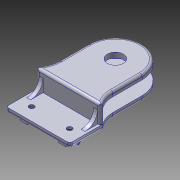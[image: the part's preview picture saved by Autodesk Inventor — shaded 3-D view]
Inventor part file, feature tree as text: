
AUTODESK INVENTOR PART (.ipt)
format: ipt  version: 2013 (Build 170138000, 138)  size: 346,112 bytes
history: native  units: mm
features: extrude x8, sketch x8, fillet x4, hole x1, chamfer x1, mirror x1
ambient origin geometry x8: Origin, YZ Plane, XZ Plane, XY Plane, X Axis, Y Axis, Z Axis, Center Point
bodies: Solid1 (feature_tree)
feature tree (23):
  extrude  "Extrusion1"  Depth=17.5mm
  sketch  "Sketch2"  dims[d3=6.35mm d4=10.5mm]
  extrude  "Extrusion2"  Depth=10.5mm
  extrude  "Extrusion3"  Depth=2.0mm
  extrude  "Extrusion4"  Depth=25.0mm
  sketch  "Sketch6"  dims[d12=1.0mm d13=0.0mm d14=2.0mm]
  hole  "Hole1"  [1 undecoded]
  extrude  "Extrusion5"  Depth=5.0mm
  extrude  "Extrusion6"  Depth=5.0mm
  extrude  "Extrusion7"  Depth=1.0mm TaperAngle=0.0deg
  chamfer  "Chamfer1"  Distance=0.5mm
  mirror  "Mirror1"
  fillet  "Fillet1"  Radius=1.0mm
  fillet  "Fillet2"  Radius=1.0mm
  fillet  "Fillet3"  Radius=1.0mm
  extrude  "Extrusion8"  Depth=1.0mm TaperAngle=45.0deg
  fillet  "Fillet4"  Radius=10.5mm
  sketch  "Sketch1"  dims[d0=21.0mm d2=17.5mm]
  sketch  "Sketch3"  dims[d5=9.35mm d6=0.0mm d7=2.0mm]
  sketch  "Sketch4"  dims[d8=2.0mm d9=0.0mm d10=25.0mm]
  sketch  "Sketch7"  dims[d16=12.0mm d17=0.0mm d18=5.0mm]
  sketch  "Sketch8"  dims[d19=5.0mm d20=5.0mm]
  sketch  "Sketch9"  dims[d21=2.013mm d22=6.0mm d23=3.023mm d24=2.0mm d25=14.3117mm d26=8.0mm d27=20.594885mm d28=1.0mm d29=0.0mm d30=0.5mm d31=1.0mm d32=0.0mm d33=1.0mm d34=1.0mm d35=0.0mm d36=1.0mm d37=2.0mm d38=45.0deg d39=10.5mm d40=10.0mm d41=5.0mm d43=1.5mm d45=1.0mm d46=1.0mm d47=0.0mm d48=1.0mm]
note: 1 required parameter value undecoded (feature->parameter linkage not recoverable at this tier; creation-order binding heuristic only, values carry confidence <= 0.55)
